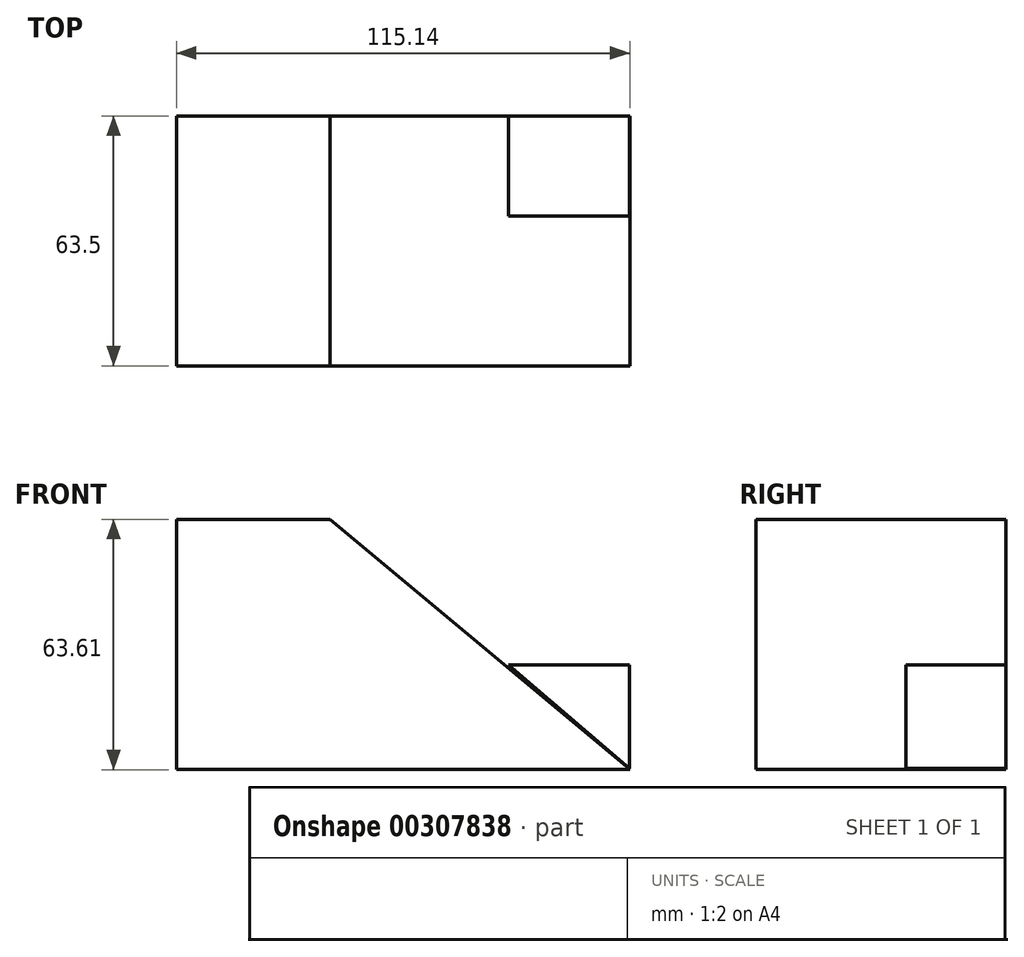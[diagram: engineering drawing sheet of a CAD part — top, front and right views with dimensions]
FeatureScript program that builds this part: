
annotation { "Feature Type Name" : "Feature", "Feature Type Description" : "" }
export const myFeature = defineFeature(function(context is Context, id is Id, definition is map)
    precondition{}
    {
        {
            var Q0;
            Q0=qCreatedBy(makeId("Front.planeOp"),FACE);
            var sketch = newSketch(context, id + "F0", { "sketchPlane" : qUnion([Q0])});
            skLineSegment(sketch, "E0", {"start": v(-53.86, 0) * mm, "end": v(-14.86, 0) * mm});
            skLineSegment(sketch, "E1", {"start": v(-53.86, 0) * mm, "end": v(-53.86, -63.6) * mm});
            skLineSegment(sketch, "E2", {"start": v(-53.86, -63.6) * mm, "end": v(61.28, -63.6) * mm});
            skLineSegment(sketch, "E3", {"start": v(-14.86, 0) * mm, "end": v(61.28, -63.6) * mm});
            skSolve(sketch);
        }
        {
            var Q0;
            Q0=makeQuery(id+"F0.imprint","IMPRINT",FACE,{"disambiguationData":[TD([[makeQuery(id+"F0.imprint","IMPRINT",EDGE,{"derivedFrom":sQuery(id+"F0.wireOp",EDGE,"E0")}),-1.0]])]});
            extrude(context, id + "F1", {"entities" : qUnion([Q0]), "depth" : 63.5 * mm});
        }
        {
            var Q0;
            Q0=qCreatedBy(makeId("Front.planeOp"),FACE);
            var sketch = newSketch(context, id + "F2", { "sketchPlane" : qUnion([Q0])});
            skLineSegment(sketch, "E4", {"start": v(61.21, -63.31) * mm, "end": v(61.21, -37.06) * mm});
            skLineSegment(sketch, "E5", {"start": v(61.21, -37.06) * mm, "end": v(30.45, -37.06) * mm});
            skLineSegment(sketch, "E6", {"start": v(61.21, -63.31) * mm, "end": v(30.45, -37.06) * mm});
            skSolve(sketch);
        }
        {
            var Q0;
            Q0=makeQuery(id+"F2.imprint","IMPRINT",FACE,{"disambiguationData":[TD([[makeQuery(id+"F2.imprint","IMPRINT",EDGE,{"derivedFrom":sQuery(id+"F2.wireOp",EDGE,"E4")}),1.0]])]});
            extrude(context, id + "F3", {"entities" : qUnion([Q0]), "depth" : 25.4 * mm});
        }
    });
